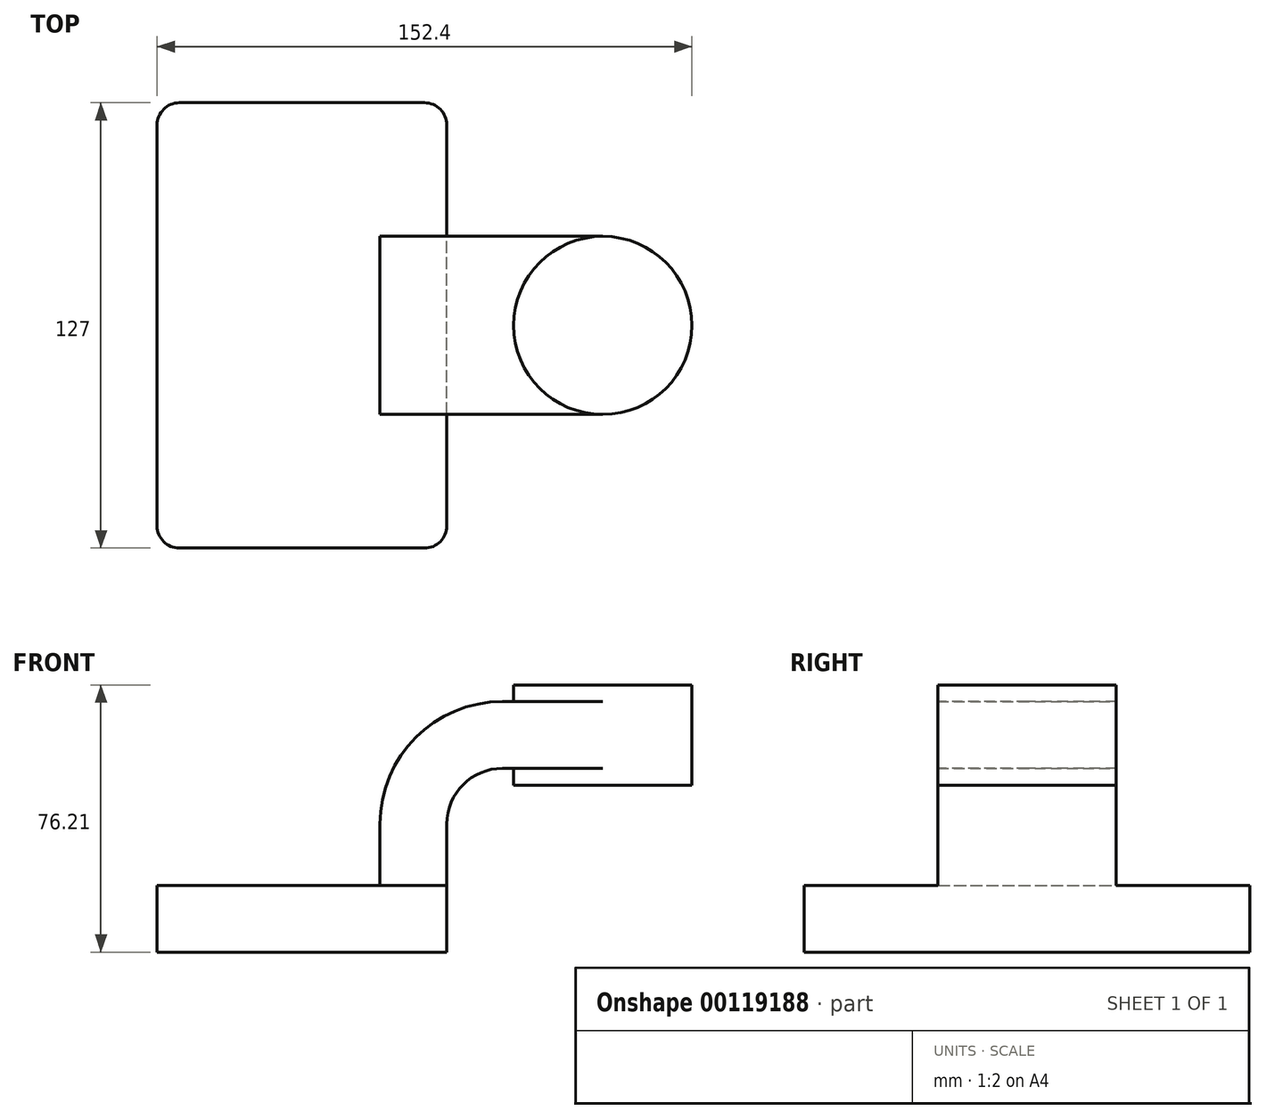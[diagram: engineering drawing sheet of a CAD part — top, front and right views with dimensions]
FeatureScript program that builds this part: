
annotation { "Feature Type Name" : "Feature", "Feature Type Description" : "" }
export const myFeature = defineFeature(function(context is Context, id is Id, definition is map)
    precondition{}
    {
        {
            var Q0;
            Q0=qCreatedBy(makeId("Front.planeOp"),FACE);
            var sketch = newSketch(context, id + "F0", { "sketchPlane" : qUnion([Q0])});
            skLineSegment(sketch, "E0.bottom", {"start": v(41.27, 9.53) * mm, "end": v(-41.28, 9.53) * mm});
            skLineSegment(sketch, "E0.top", {"start": v(41.28, -9.52) * mm, "end": v(-41.27, -9.52) * mm});
            skLineSegment(sketch, "E0.left", {"start": v(41.28, 9.53) * mm, "end": v(41.28, -9.52) * mm});
            skLineSegment(sketch, "E0.right", {"start": v(-41.28, 9.53) * mm, "end": v(-41.27, -9.52) * mm});
            skPoint(sketch, "E0.middle", {"position": v(0, 0) * mm});
            skLineSegment(sketch, "E1.bottom", {"start": v(60.33, 66.68) * mm, "end": v(111.12, 66.68) * mm});
            skLineSegment(sketch, "E1.top", {"start": v(60.33, 38.1) * mm, "end": v(111.12, 38.1) * mm});
            skLineSegment(sketch, "E1.left", {"start": v(60.33, 66.68) * mm, "end": v(60.33, 38.1) * mm});
            skLineSegment(sketch, "E1.right", {"start": v(111.12, 66.68) * mm, "end": v(111.13, 38.1) * mm});
            skPoint(sketch, "E1.middle", {"position": v(85.73, 52.39) * mm});
            skLineSegment(sketch, "E2", {"start": v(41.27, 9.53) * mm, "end": v(41.27, 27) * mm});
            skArc(sketch, "E3", {"start": v(41.27, 27) * mm, "mid": v(45.92, 38.23) * mm, "end": v(57.15, 42.88) * mm});
            skLineSegment(sketch, "E4", {"start": v(57.15, 42.88) * mm, "end": v(85.73, 42.88) * mm});
            skLineSegment(sketch, "E5.0", {"start": v(57.15, 61.93) * mm, "end": v(85.73, 61.93) * mm});
            skArc(sketch, "E5.1", {"start": v(22.22, 27) * mm, "mid": v(32.45, 51.7) * mm, "end": v(57.15, 61.93) * mm});
            skLineSegment(sketch, "E5.2", {"start": v(22.22, 9.53) * mm, "end": v(22.22, 27) * mm});
            skLineSegment(sketch, "E6", {"start": v(85.73, 38.1) * mm, "end": v(85.73, 66.68) * mm});
            skFitSpline(sketch, "E7", {"points": [v(-41.28, 9.53) * mm, v(57.15, 61.93) * mm], "startDerivative": vector(47.42, 120.78) * mm, "endDerivative": vector(122.2, -3.52) * mm});
            skSolve(sketch);
        }
        {
            var Q0;
            Q0=makeQuery(id+"F0.imprint","IMPRINT",FACE,{"disambiguationData":[TD([[makeQuery(id+"F0.imprint","IMPRINT",EDGE,{"derivedFrom":sQuery(id+"F0.wireOp",EDGE,"E0.top")}),-1.0]])]});
            extrude(context, id + "F1", {"entities" : qUnion([Q0]), "endBound" : BoundingType.SYMMETRIC, "depth" : 127 * mm});
        }
        {
            var Q0;
            {var subQ1=sQuery(id+"F0.wireOp",EDGE,"E2");Q0=makeQuery(id+"F0.imprint","IMPRINT",FACE,{"disambiguationData":[TD([[makeQuery(id+"F0.imprint","IMPRINT",EDGE,{"derivedFrom":subQ1}),1.0]])]});}
            var Q1;
            {var subQ0=sQuery(id+"F0.wireOp",EDGE,"E5.0");var subQ1=sQuery(id+"F0.wireOp",EDGE,"E1.left");var subQ2=makeQuery(id+"F0.imprint","INTERSECT",VERTEX,{"derivedFrom":[subQ1,subQ0]});Q1=makeQuery(id+"F0.imprint","IMPRINT",FACE,{"disambiguationData":[TD([[makeQuery(id+"F0.imprint","IMPRINT",EDGE,{"disambiguationData":[TD([[subQ2,-1.0]])],"derivedFrom":subQ1}),1.0]])]});}
            extrude(context, id + "F2", {"entities" : qUnion([Q0, Q1]), "operationType" : NewBodyOperationType.ADD, "endBound" : BoundingType.SYMMETRIC, "depth" : 50.8 * mm});
        }
        {
            var Q0;
            Q0=makeQuery(id+"F0.imprint","IMPRINT",FACE,{"disambiguationData":[TD([[makeQuery(id+"F0.imprint","IMPRINT",EDGE,{"derivedFrom":sQuery(id+"F0.wireOp",EDGE,"E5.1")}),1.0]])]});
            extrude(context, id + "F3", {"entities" : qUnion([Q0]), "operationType" : NewBodyOperationType.ADD, "endBound" : BoundingType.SYMMETRIC, "depth" : 25.4 * mm});
        }
        {
            var Q0;
            {var subQ0=sQuery(id+"F0.wireOp",EDGE,"E1.right");Q0=makeQuery(id+"F0.imprint","IMPRINT",FACE,{"disambiguationData":[TD([[makeQuery(id+"F0.imprint","IMPRINT",EDGE,{"derivedFrom":subQ0}),-1.0]])]});}
            var Q1;
            Q1=sQuery(id+"F0.wireOp",EDGE,"E6");
            revolve(context, id + "F4", {"operationType" : NewBodyOperationType.ADD, "entities" : qUnion([Q0]), "axis" : qUnion([Q1]), "revolveType" : RevolveType.FULL});
        }
        {
            var Q0;
            Q0=makeQuery(id+"F1.opExtrude","CAP_EDGE",EDGE,{"disambiguationData":[OSD([sQuery(id+"F0.wireOp",EDGE,"E0.right")])],"isStart":false});
            var Q1;
            Q1=makeQuery(id+"F1.opExtrude","CAP_EDGE",EDGE,{"disambiguationData":[OSD([sQuery(id+"F0.wireOp",EDGE,"E0.left")])],"isStart":false});
            var Q2;
            Q2=makeQuery(id+"F1.opExtrude","CAP_EDGE",EDGE,{"disambiguationData":[OSD([sQuery(id+"F0.wireOp",EDGE,"E0.left")])],"isStart":true});
            var Q3;
            Q3=makeQuery(id+"F1.opExtrude","CAP_EDGE",EDGE,{"disambiguationData":[OSD([sQuery(id+"F0.wireOp",EDGE,"E0.right")])],"isStart":true});
            fillet(context, id + "F5", {"entities" : qUnion([Q0, Q1, Q2, Q3]), "radius" : 6.35 * mm, "tangentPropagation" : true, "allowEdgeOverflow" : false});
        }
    });
